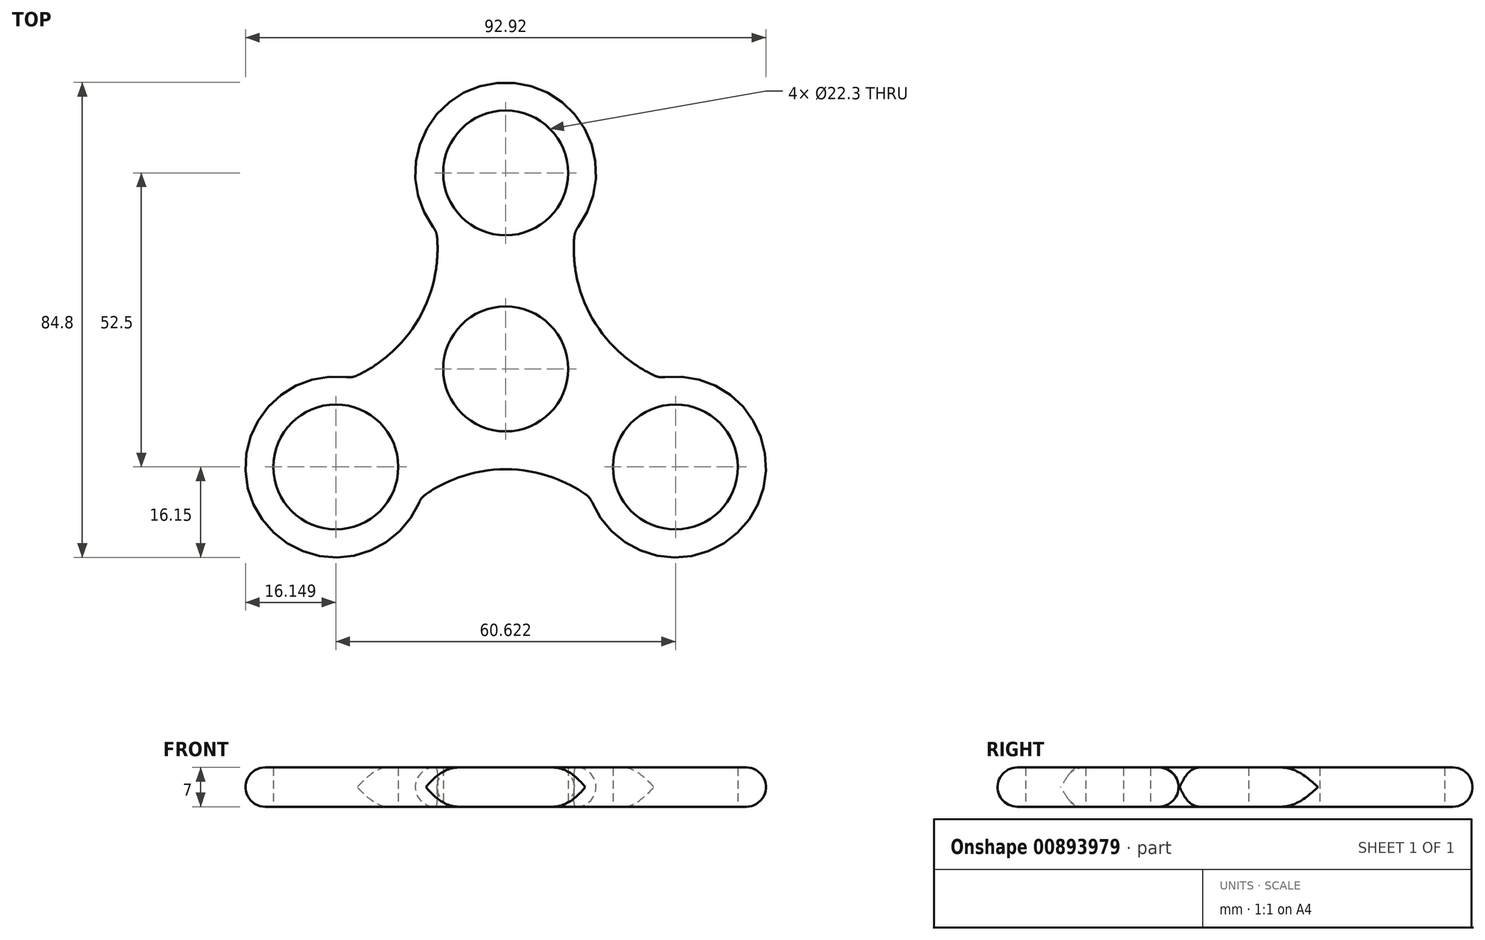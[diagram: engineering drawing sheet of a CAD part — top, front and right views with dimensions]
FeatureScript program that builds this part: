
annotation { "Feature Type Name" : "Feature", "Feature Type Description" : "" }
export const myFeature = defineFeature(function(context is Context, id is Id, definition is map)
    precondition{}
    {
        {
            var Q0;
            Q0=qCreatedBy(makeId("Top.planeOp"),FACE);
            var sketch = newSketch(context, id + "F0", { "sketchPlane" : qUnion([Q0])});
            skCircle(sketch, "E0", {"center": v(0, 0) * mm, "radius": 11.15 * mm});
            skLineSegment(sketch, "E1", {"start": v(0, 0) * mm, "end": v(0, 35) * mm, "construction": true});
            skCircle(sketch, "E2", {"center": v(0, 35) * mm, "radius": 11.15 * mm});
            skCircle(sketch, "E3.1.0", {"center": v(-30.31, -17.5) * mm, "radius": 11.15 * mm});
            skCircle(sketch, "E3.2.0", {"center": v(30.31, -17.5) * mm, "radius": 11.15 * mm});
            skArc(sketch, "E4.0", {"start": v(12.36, 24.6) * mm, "mid": v(0, 51.15) * mm, "end": v(-12.36, 24.6) * mm});
            skArc(sketch, "E5.0", {"start": v(15.13, -23.01) * mm, "mid": v(44.3, -25.58) * mm, "end": v(27.5, -1.6) * mm});
            skArc(sketch, "E6.0", {"start": v(-27.5, -1.6) * mm, "mid": v(-44.3, -25.57) * mm, "end": v(-15.13, -23.01) * mm});
            skLineSegment(sketch, "E7", {"start": v(0, 35) * mm, "end": v(16.15, 35) * mm, "construction": true});
            skLineSegment(sketch, "E8", {"start": v(0, 0) * mm, "end": v(30.31, -17.5) * mm, "construction": true});
            skLineSegment(sketch, "E9", {"start": v(30.31, -17.5) * mm, "end": v(38.39, -3.51) * mm, "construction": true});
            skArc(sketch, "E10", {"start": v(12.36, 24.6) * mm, "mid": v(15.51, 8.96) * mm, "end": v(27.5, -1.6) * mm});
            skArc(sketch, "E11.1.0", {"start": v(-27.5, -1.6) * mm, "mid": v(-15.51, 8.96) * mm, "end": v(-12.36, 24.6) * mm});
            skArc(sketch, "E11.2.0", {"start": v(15.13, -23.01) * mm, "mid": v(0, -17.91) * mm, "end": v(-15.13, -23.01) * mm});
            skPoint(sketch, "E12.orphan", {"position": v(-16.15, 35) * mm});
            skPoint(sketch, "E13.orphan", {"position": v(-38.39, -3.51) * mm});
            skPoint(sketch, "E14.orphan", {"position": v(-22.24, -31.49) * mm});
            skPoint(sketch, "E15.orphan", {"position": v(22.24, -31.49) * mm});
            skSolve(sketch);
        }
        {
            var Q0;
            Q0 = qSketchRegion(id + "F0", true);
            extrude(context, id + "F1", {"entities" : qUnion([Q0]), "depth" : 7 * mm, "offsetDistance" : 25 * mm});
        }
        {
            var Q0;
            Q0=makeQuery(id+"F1.opExtrude","SWEPT_FACE",FACE,{"disambiguationData":[OSD([sQuery(id+"F0.wireOp",EDGE,"E5.0")])]});
            var Q1;
            Q1=makeQuery(id+"F1.opExtrude","SWEPT_FACE",FACE,{"disambiguationData":[OSD([sQuery(id+"F0.wireOp",EDGE,"E6.0")])]});
            var Q2;
            Q2=makeQuery(id+"F1.opExtrude","SWEPT_FACE",FACE,{"disambiguationData":[OSD([sQuery(id+"F0.wireOp",EDGE,"E4.0")])]});
            fillet(context, id + "F2", {"entities" : qUnion([Q0, Q1, Q2]), "radius" : 3.5 * mm, "tangentPropagation" : true, "allowEdgeOverflow" : false});
        }
    });
